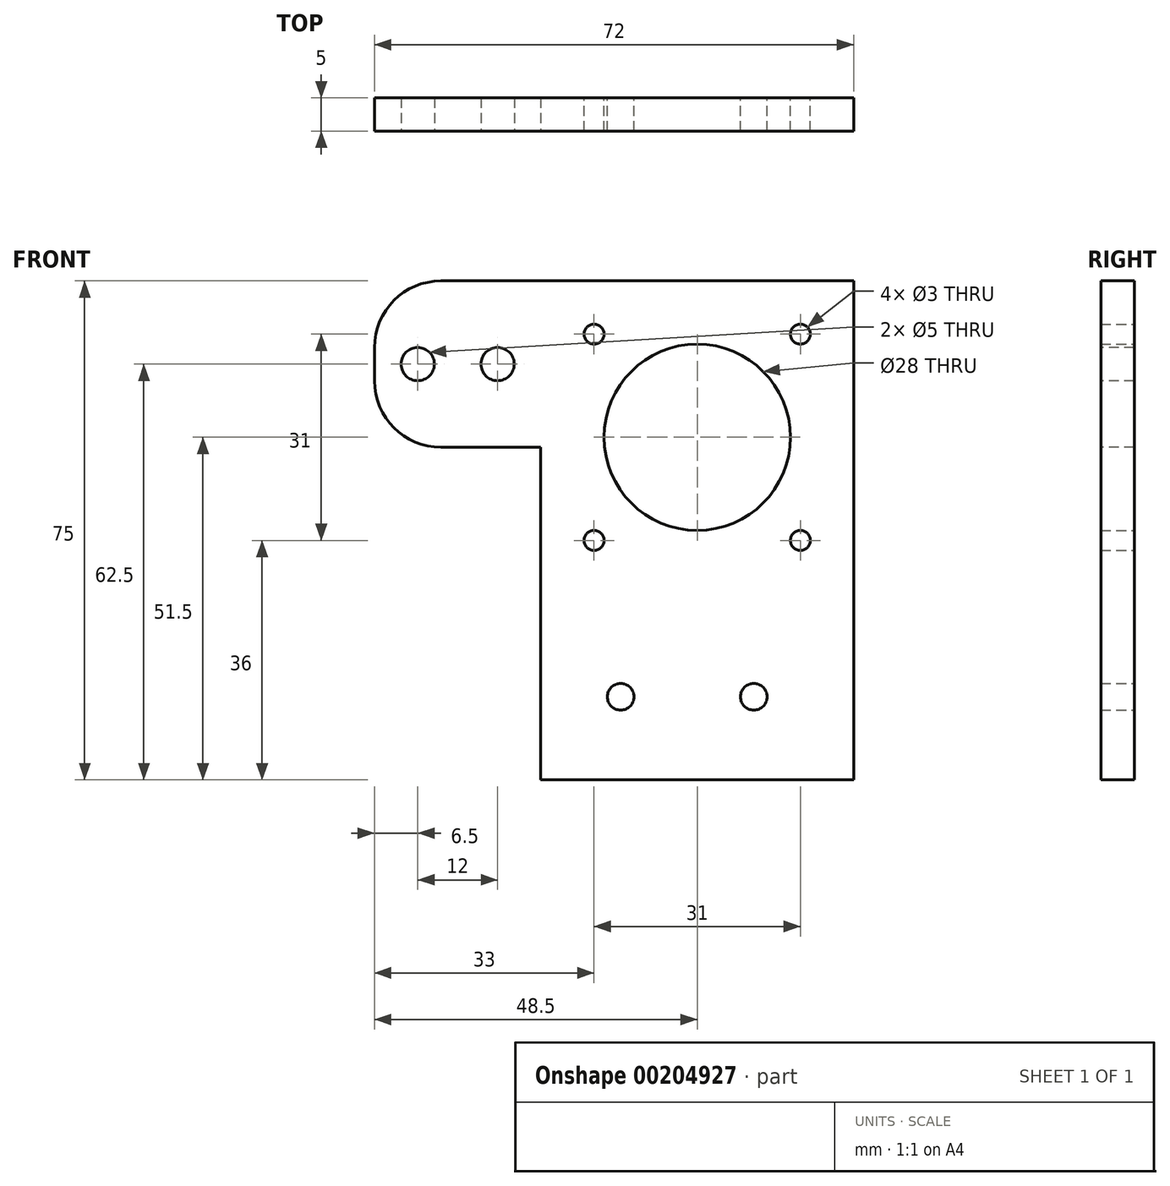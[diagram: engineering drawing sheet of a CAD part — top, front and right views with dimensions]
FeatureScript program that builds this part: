
annotation { "Feature Type Name" : "Feature", "Feature Type Description" : "" }
export const myFeature = defineFeature(function(context is Context, id is Id, definition is map)
    precondition{}
    {
        {
            var Q0;
            Q0=qCreatedBy(makeId("Front.planeOp"),FACE);
            var sketch = newSketch(context, id + "F0", { "sketchPlane" : qUnion([Q0])});
            skLineSegment(sketch, "E0.bottom", {"start": v(0, 25) * mm, "end": v(47, 25) * mm});
            skLineSegment(sketch, "E0.top", {"start": v(0, 75) * mm, "end": v(47, 75) * mm});
            skLineSegment(sketch, "E0.left", {"start": v(0, 25) * mm, "end": v(0, 75) * mm});
            skLineSegment(sketch, "E0.right", {"start": v(47, 25) * mm, "end": v(47, 75) * mm});
            skLineSegment(sketch, "E1.bottom", {"start": v(8, 36) * mm, "end": v(39, 36) * mm, "construction": true});
            skLineSegment(sketch, "E1.top", {"start": v(8, 67) * mm, "end": v(39, 67) * mm, "construction": true});
            skLineSegment(sketch, "E1.left", {"start": v(8, 36) * mm, "end": v(8, 67) * mm, "construction": true});
            skLineSegment(sketch, "E1.right", {"start": v(39, 36) * mm, "end": v(39, 67) * mm, "construction": true});
            skCircle(sketch, "E2", {"center": v(8, 67) * mm, "radius": 1.5 * mm});
            skCircle(sketch, "E3", {"center": v(39, 67) * mm, "radius": 1.5 * mm});
            skCircle(sketch, "E4", {"center": v(39, 36) * mm, "radius": 1.5 * mm});
            skCircle(sketch, "E5", {"center": v(8, 36) * mm, "radius": 1.5 * mm});
            skLineSegment(sketch, "E6", {"start": v(8, 36) * mm, "end": v(39, 67) * mm});
            skPoint(sketch, "E7", {"position": v(23.5, 51.5) * mm});
            skLineSegment(sketch, "E8", {"start": v(23.5, 51.5) * mm, "end": v(53.5, 51.5) * mm, "construction": true});
            skCircle(sketch, "E9", {"center": v(53.5, 51.5) * mm, "radius": 4 * mm, "construction": true});
            skCircle(sketch, "E10", {"center": v(53.5, 51.5) * mm, "radius": 12 * mm, "construction": true});
            skLineSegment(sketch, "E11.top", {"start": v(0, 0) * mm, "end": v(47, 0) * mm});
            skLineSegment(sketch, "E11.left", {"start": v(0, 25) * mm, "end": v(0, 0) * mm});
            skLineSegment(sketch, "E11.right", {"start": v(47, 25) * mm, "end": v(47, 0) * mm});
            skCircle(sketch, "E12", {"center": v(23.5, 51.5) * mm, "radius": 14 * mm});
            skLineSegment(sketch, "E13", {"start": v(53.5, 51.5) * mm, "end": v(53.5, 42.5) * mm});
            skCircle(sketch, "E14", {"center": v(53.5, 42.5) * mm, "radius": 2.5 * mm, "construction": true});
            skLineSegment(sketch, "E15", {"start": v(53.5, 51.5) * mm, "end": v(65.5, 51.5) * mm, "construction": true});
            skLineSegment(sketch, "E16", {"start": v(65.5, 51.5) * mm, "end": v(65.5, 0) * mm, "construction": true});
            skLineSegment(sketch, "E17", {"start": v(65.5, 0) * mm, "end": v(47, 0) * mm});
            skLineSegment(sketch, "E18", {"start": v(65.5, 51.5) * mm, "end": v(65.5, 75) * mm, "construction": true});
            skLineSegment(sketch, "E19", {"start": v(65.5, 75) * mm, "end": v(47, 75) * mm, "construction": true});
            skLineSegment(sketch, "E20", {"start": v(47, 12.5) * mm, "end": v(0, 12.5) * mm});
            skLineSegment(sketch, "E21", {"start": v(47, 12.5) * mm, "end": v(65.5, 12.5) * mm, "construction": true});
            skCircle(sketch, "E22", {"center": v(12, 12.5) * mm, "radius": 2 * mm});
            skCircle(sketch, "E23", {"center": v(32, 12.5) * mm, "radius": 2 * mm});
            skCircle(sketch, "E24", {"center": v(53.5, 12.5) * mm, "radius": 2 * mm, "construction": true});
            skLineSegment(sketch, "E25", {"start": v(61.5, 75) * mm, "end": v(61.5, 70) * mm});
            skLineSegment(sketch, "E26", {"start": v(61.5, 70) * mm, "end": v(61.5, 63) * mm});
            skCircle(sketch, "E27", {"center": v(61.5, 70) * mm, "radius": 1.5 * mm, "construction": true});
            skCircle(sketch, "E28", {"center": v(61.5, 63) * mm, "radius": 1.5 * mm, "construction": true});
            skSolve(sketch);
        }
        {
            var Q0;
            Q0=makeQuery(id+"F0.imprint","IMPRINT",FACE,{"disambiguationData":[TD([[makeQuery(id+"F0.imprint","IMPRINT",EDGE,{"derivedFrom":sQuery(id+"F0.wireOp",EDGE,"E0.top")}),-1.0]])]});
            var Q1;
            {var subQ5=sQuery(id+"F0.wireOp",EDGE,"E0.bottom");Q1=makeQuery(id+"F0.imprint","IMPRINT",FACE,{"disambiguationData":[TD([[makeQuery(id+"F0.imprint","IMPRINT",EDGE,{"derivedFrom":subQ5}),-1.0]])]});}
            var Q2;
            {var subQ5=sQuery(id+"F0.wireOp",EDGE,"E11.top");Q2=makeQuery(id+"F0.imprint","IMPRINT",FACE,{"disambiguationData":[TD([[makeQuery(id+"F0.imprint","IMPRINT",EDGE,{"derivedFrom":subQ5}),1.0]])]});}
            extrude(context, id + "F1", {"entities" : qUnion([Q0, Q1, Q2]), "depth" : 5 * mm});
        }
        {
            var Q0;
            Q0=makeQuery(id+"F1.opExtrude","CAP_FACE",FACE,{"disambiguationData":[OSD([sQuery(id+"F0.wireOp",EDGE,"E0.top"),sQuery(id+"F0.wireOp",EDGE,"E0.left"),sQuery(id+"F0.wireOp",EDGE,"E0.right"),sQuery(id+"F0.wireOp",EDGE,"E2"),sQuery(id+"F0.wireOp",EDGE,"E3"),sQuery(id+"F0.wireOp",EDGE,"E4"),sQuery(id+"F0.wireOp",EDGE,"E5"),sQuery(id+"F0.wireOp",EDGE,"E11.top"),sQuery(id+"F0.wireOp",EDGE,"E11.left"),sQuery(id+"F0.wireOp",EDGE,"E11.right"),sQuery(id+"F0.wireOp",EDGE,"E12"),sQuery(id+"F0.wireOp",EDGE,"E22"),sQuery(id+"F0.wireOp",EDGE,"E23")])],"isStart":false});
            var sketch = newSketch(context, id + "F2", { "sketchPlane" : qUnion([Q0])});
            skLineSegment(sketch, "E29.bottom", {"start": v(47, 75) * mm, "end": v(72, 75) * mm});
            skLineSegment(sketch, "E29.top", {"start": v(47, 50) * mm, "end": v(72, 50) * mm});
            skLineSegment(sketch, "E29.left", {"start": v(47, 75) * mm, "end": v(47, 50) * mm});
            skLineSegment(sketch, "E29.right", {"start": v(72, 75) * mm, "end": v(72, 50) * mm});
            skLineSegment(sketch, "E30.bottom", {"start": v(0, 75) * mm, "end": v(-15, 75) * mm});
            skLineSegment(sketch, "E30.top", {"start": v(0, 50) * mm, "end": v(-15, 50) * mm});
            skLineSegment(sketch, "E30.left", {"start": v(0, 75) * mm, "end": v(0, 50) * mm});
            skLineSegment(sketch, "E30.right", {"start": v(-25, 65) * mm, "end": v(-25, 60) * mm});
            skLineSegment(sketch, "E31", {"start": v(0, 62.5) * mm, "end": v(-25, 62.5) * mm});
            skLineSegment(sketch, "E32", {"start": v(47, 62.5) * mm, "end": v(72, 62.5) * mm});
            skCircle(sketch, "E33", {"center": v(-6.5, 62.5) * mm, "radius": 2.5 * mm});
            skCircle(sketch, "E34", {"center": v(-6.5, 62.5) * mm, "radius": 7 * mm});
            skCircle(sketch, "E35", {"center": v(-18.5, 62.5) * mm, "radius": 2.5 * mm});
            skPoint(sketch, "E36.visualSharp", {"position": v(-25, 75) * mm});
            skArc(sketch, "E36.filletArc", {"start": v(-15, 75) * mm, "mid": v(-22.07, 72.07) * mm, "end": v(-25, 65) * mm});
            skPoint(sketch, "E37.visualSharp", {"position": v(-25, 50) * mm});
            skArc(sketch, "E37.filletArc", {"start": v(-25, 60) * mm, "mid": v(-22.07, 52.93) * mm, "end": v(-15, 50) * mm});
            skSolve(sketch);
        }
        {
            var Q0;
            {var subQ6=sQuery(id+"F2.wireOp",EDGE,"E30.bottom");Q0=makeQuery(id+"F2.imprint","IMPRINT",FACE,{"disambiguationData":[TD([[makeQuery(id+"F2.imprint","IMPRINT",EDGE,{"derivedFrom":subQ6}),1.0]])]});}
            var Q1;
            {var subQ6=sQuery(id+"F2.wireOp",EDGE,"E30.top");Q1=makeQuery(id+"F2.imprint","IMPRINT",FACE,{"disambiguationData":[TD([[makeQuery(id+"F2.imprint","IMPRINT",EDGE,{"derivedFrom":subQ6}),-1.0]])]});}
            var Q2;
            {var subQ1=sQuery(id+"F2.wireOp",EDGE,"E31");var subQ4=sQuery(id+"F2.wireOp",EDGE,"E30.left");var subQ5=makeQuery(id+"F2.imprint","INTERSECT",VERTEX,{"derivedFrom":[subQ4,subQ1]});Q2=makeQuery(id+"F2.imprint","IMPRINT",FACE,{"disambiguationData":[TD([[makeQuery(id+"F2.imprint","IMPRINT",EDGE,{"disambiguationData":[TD([[subQ5,1.0]])],"derivedFrom":subQ4}),1.0]])]});}
            var Q3;
            {var subQ1=sQuery(id+"F2.wireOp",EDGE,"E31");var subQ4=sQuery(id+"F2.wireOp",EDGE,"E30.left");var subQ5=makeQuery(id+"F2.imprint","INTERSECT",VERTEX,{"derivedFrom":[subQ4,subQ1]});Q3=makeQuery(id+"F2.imprint","IMPRINT",FACE,{"disambiguationData":[TD([[makeQuery(id+"F2.imprint","IMPRINT",EDGE,{"disambiguationData":[TD([[subQ5,-1.0]])],"derivedFrom":subQ4}),1.0]])]});}
            extrude(context, id + "F3", {"entities" : qUnion([Q0, Q1, Q2, Q3]), "operationType" : NewBodyOperationType.ADD, "oppositeDirection" : true, "depth" : 5 * mm});
        }
        {
            var Q0;
            Q0=makeQuery(id+"F1.opExtrude","SWEPT_FACE",FACE,{"disambiguationData":[OSD([sQuery(id+"F0.wireOp",EDGE,"E0.right"),sQuery(id+"F0.wireOp",EDGE,"E11.right")])]});
            cPlane(context, id + "F4", {"entities" : qUnion([Q0]), "cplaneType" : CPlaneType.OFFSET, "offset" : (47 / 2) * mm, "oppositeDirection" : true, "width" : 150 * mm, "height" : 150 * mm});
        }
    });
